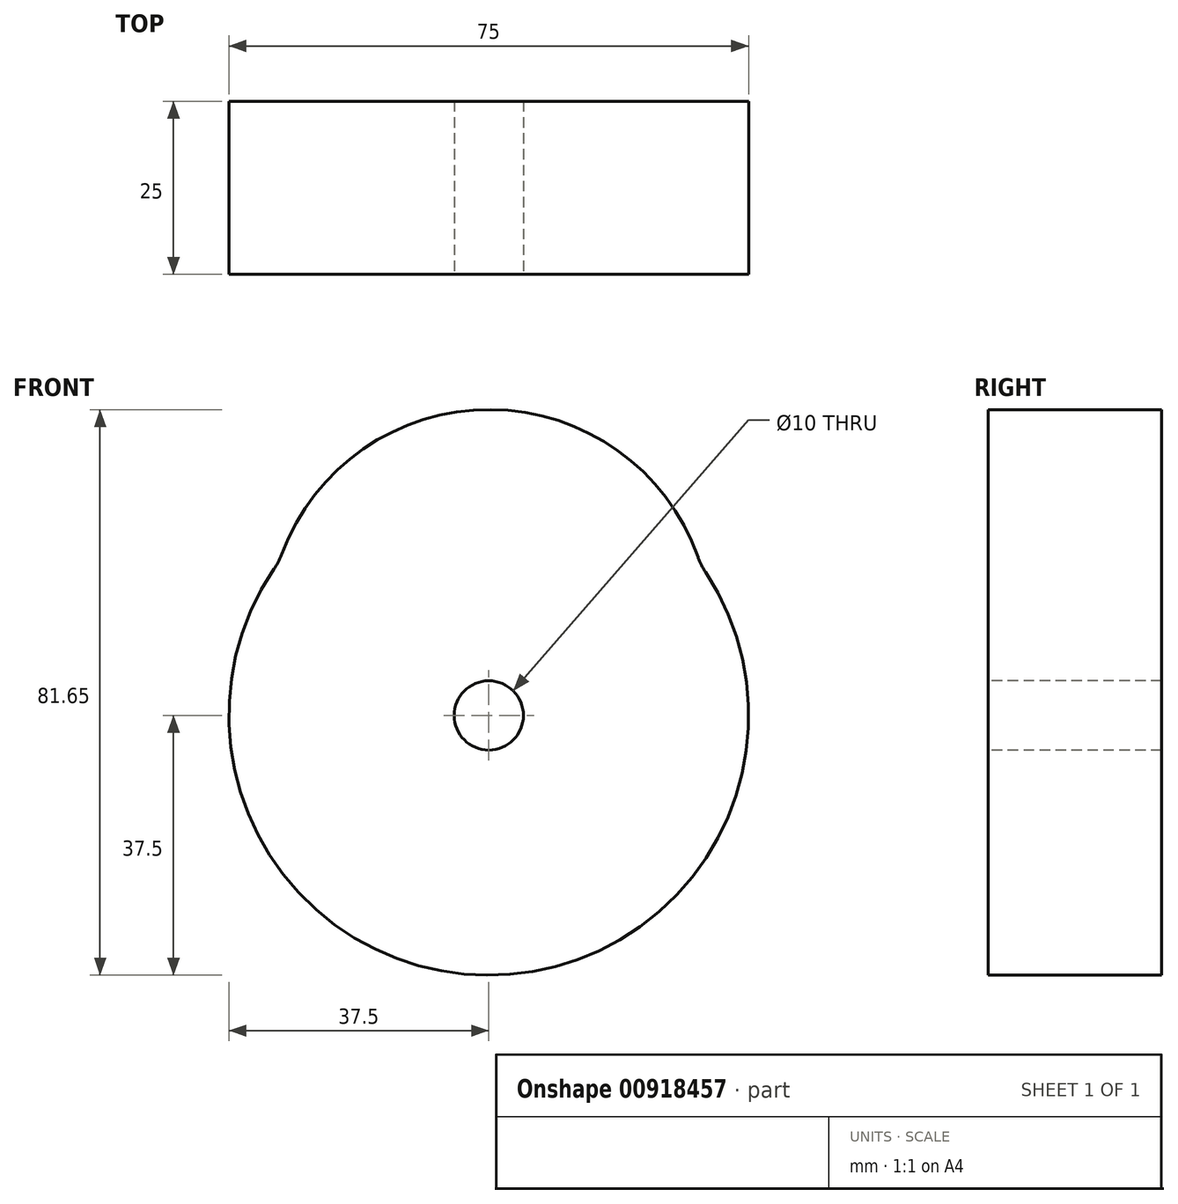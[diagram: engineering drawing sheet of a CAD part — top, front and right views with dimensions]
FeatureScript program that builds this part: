
annotation { "Feature Type Name" : "Feature", "Feature Type Description" : "" }
export const myFeature = defineFeature(function(context is Context, id is Id, definition is map)
    precondition{}
    {
        {
            var Q0;
            Q0=qCreatedBy(makeId("Front.planeOp"),FACE);
            var sketch = newSketch(context, id + "F0", { "sketchPlane" : qUnion([Q0])});
            skArc(sketch, "E0", {"start": v(-30.28, 22.13) * mm, "mid": v(-0.25, -37.5) * mm, "end": v(30.57, 21.71) * mm});
            skArc(sketch, "E1", {"start": v(30.57, 21.71) * mm, "mid": v(0.3, 44.15) * mm, "end": v(-30.28, 22.13) * mm});
            skSolve(sketch);
        }
        {
            var Q0;
            Q0=makeQuery(id+"F0.imprint","IMPRINT",FACE,{"disambiguationData":[TD([[makeQuery(id+"F0.imprint","IMPRINT",EDGE,{"derivedFrom":sQuery(id+"F0.wireOp",EDGE,"E0")}),1.0]])]});
            extrude(context, id + "F1", {"entities" : qUnion([Q0]), "endBound" : BoundingType.SYMMETRIC, "depth" : 25 * mm, "offsetDistance" : 25 * mm});
        }
        {
            var Q0;
            {var subQ0=sQuery(id+"F0.wireOp",EDGE,"E1");var subQ1=sQuery(id+"F0.wireOp",EDGE,"E0");Q0=makeQuery(id+"F1.opExtrude","SWEPT_EDGE",EDGE,{"disambiguationData":[OSD([subQ1,subQ0]),TDD([makeQuery(id+"F0.imprint","INTERSECT",VERTEX,{"disambiguationData":[OD(1.0)],"derivedFrom":[subQ1,subQ0]})])]});}
            var Q1;
            {var subQ0=sQuery(id+"F0.wireOp",EDGE,"E1");var subQ1=sQuery(id+"F0.wireOp",EDGE,"E0");Q1=makeQuery(id+"F1.opExtrude","SWEPT_EDGE",EDGE,{"disambiguationData":[OSD([subQ1,subQ0]),TDD([makeQuery(id+"F0.imprint","INTERSECT",VERTEX,{"disambiguationData":[OD(0.0)],"derivedFrom":[subQ1,subQ0]})])]});}
            fillet(context, id + "F2", {"entities" : qUnion([Q0, Q1]), "radius" : 10 * mm, "tangentPropagation" : true, "allowEdgeOverflow" : false});
        }
        {
            var Q0;
            Q0=makeQuery(id+"F1.opExtrude","CAP_FACE",FACE,{"disambiguationData":[OSD([sQuery(id+"F0.wireOp",EDGE,"E0"),sQuery(id+"F0.wireOp",EDGE,"E1")])],"isStart":false});
            var sketch = newSketch(context, id + "F3", { "sketchPlane" : qUnion([Q0])});
            skCircle(sketch, "E2", {"center": v(0, 0) * mm, "radius": 5 * mm});
            skSolve(sketch);
        }
        {
            var Q0;
            Q0=makeQuery(id+"F3.imprint","IMPRINT",FACE,{"disambiguationData":[TD([[makeQuery(id+"F3.imprint","IMPRINT",EDGE,{"derivedFrom":sQuery(id+"F3.wireOp",EDGE,"E2")}),1.0]])]});
            extrude(context, id + "F4", {"entities" : qUnion([Q0]), "operationType" : NewBodyOperationType.REMOVE, "endBound" : BoundingType.THROUGH_ALL, "oppositeDirection" : true, "depth" : 25 * mm, "offsetDistance" : 25 * mm});
        }
    });
